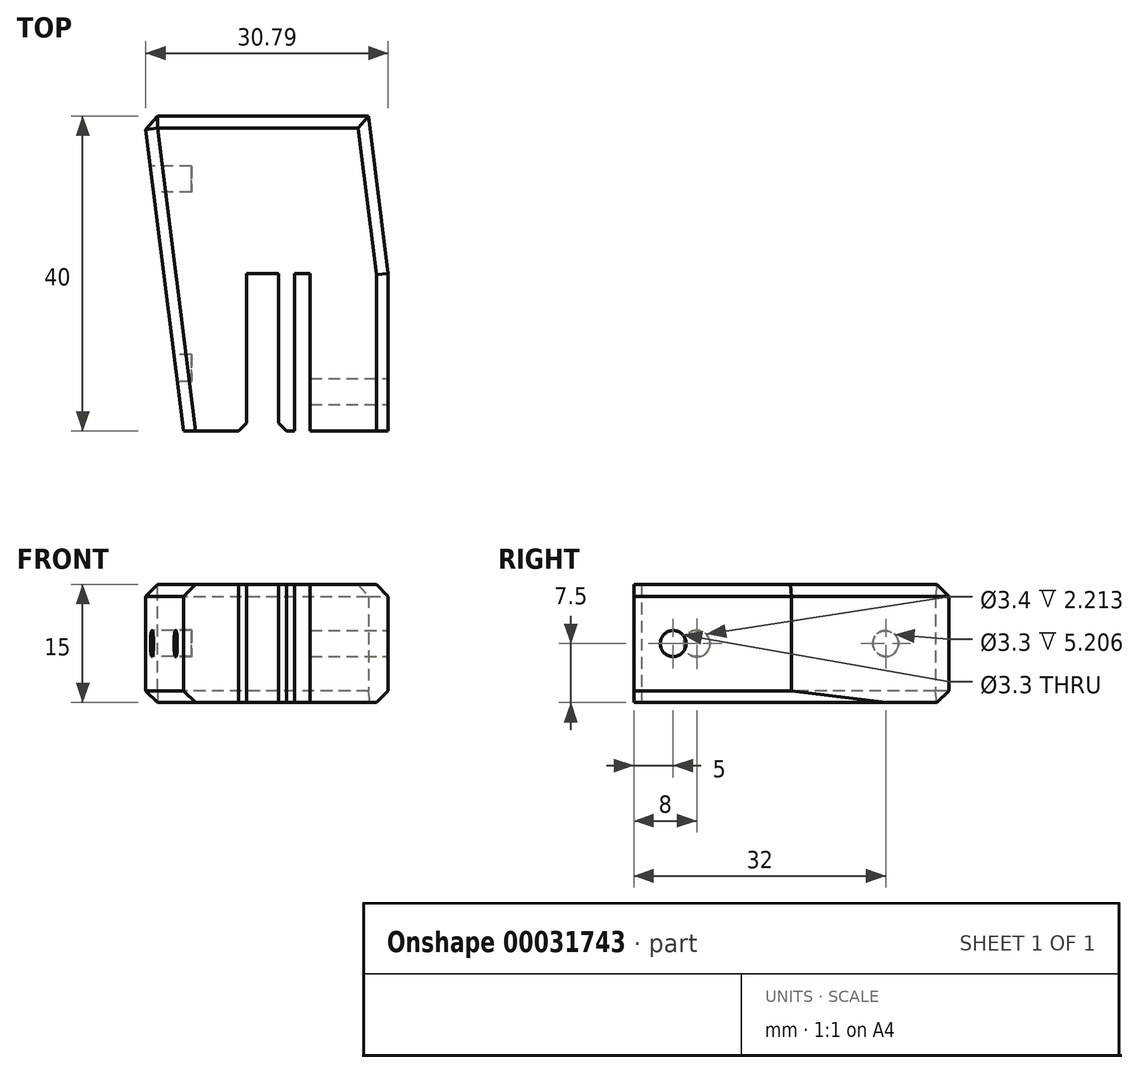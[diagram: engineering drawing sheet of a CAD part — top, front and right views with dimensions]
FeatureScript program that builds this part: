
annotation { "Feature Type Name" : "Feature", "Feature Type Description" : "" }
export const myFeature = defineFeature(function(context is Context, id is Id, definition is map)
    precondition{}
    {
        {
            var Q0;
            Q0=qCreatedBy(makeId("Top.planeOp"),FACE);
            var sketch = newSketch(context, id + "F0", { "sketchPlane" : qUnion([Q0])});
            skLineSegment(sketch, "E0", {"start": v(3, 40) * mm, "end": v(34, 40) * mm});
            skLineSegment(sketch, "E1", {"start": v(34, 40) * mm, "end": v(34, 0) * mm});
            skLineSegment(sketch, "E2", {"start": v(34, 0) * mm, "end": v(24.1, 0) * mm});
            skLineSegment(sketch, "E3", {"start": v(24.1, 0) * mm, "end": v(24.1, 20) * mm});
            skLineSegment(sketch, "E4", {"start": v(24.1, 20) * mm, "end": v(22.1, 20) * mm});
            skLineSegment(sketch, "E5", {"start": v(22.1, 20) * mm, "end": v(22.1, 0) * mm});
            skLineSegment(sketch, "E6", {"start": v(22.1, 0) * mm, "end": v(20.1, 0) * mm});
            skLineSegment(sketch, "E7", {"start": v(20.1, 0) * mm, "end": v(20.1, 20) * mm});
            skLineSegment(sketch, "E8", {"start": v(20.1, 20) * mm, "end": v(16, 20) * mm});
            skLineSegment(sketch, "E9", {"start": v(16, 20) * mm, "end": v(16, 0) * mm});
            skLineSegment(sketch, "E10", {"start": v(16, 0) * mm, "end": v(8, 0) * mm});
            skLineSegment(sketch, "E11", {"start": v(8, 0) * mm, "end": v(3, 40) * mm});
            skPoint(sketch, "E12.orphan", {"position": v(0, 0) * mm});
            skSolve(sketch);
        }
        {
            var Q0;
            Q0 = qSketchRegion(id + "F0", true);
            extrude(context, id + "F1", {"entities" : qUnion([Q0]), "depth" : 15 * mm});
        }
        {
            var Q0;
            Q0=qCreatedBy(makeId("Right.planeOp"),FACE);
            var sketch = newSketch(context, id + "F2", { "sketchPlane" : qUnion([Q0])});
            skCircle(sketch, "E13", {"center": v(32, 7.5) * mm, "radius": 1.65 * mm});
            skCircle(sketch, "E14", {"center": v(8, 7.5) * mm, "radius": 1.7 * mm});
            skSolve(sketch);
        }
        {
            var Q0;
            Q0=makeQuery(id+"F2.imprint","IMPRINT",FACE,{"disambiguationData":[TD([[makeQuery(id+"F2.imprint","IMPRINT",EDGE,{"derivedFrom":sQuery(id+"F2.wireOp",EDGE,"E13")}),1.0]])]});
            var Q1;
            Q1=makeQuery(id+"F2.imprint","IMPRINT",FACE,{"disambiguationData":[TD([[makeQuery(id+"F2.imprint","IMPRINT",EDGE,{"derivedFrom":sQuery(id+"F2.wireOp",EDGE,"E14")}),1.0]])]});
            extrude(context, id + "F3", {"entities" : qUnion([Q0, Q1]), "operationType" : NewBodyOperationType.REMOVE, "depth" : 9 * mm});
        }
        {
            var Q0;
            Q0=makeQuery(id+"F1.opExtrude","CAP_FACE",FACE,{"disambiguationData":[OSD([sQuery(id+"F0.wireOp",EDGE,"E0"),sQuery(id+"F0.wireOp",EDGE,"E1"),sQuery(id+"F0.wireOp",EDGE,"E2"),sQuery(id+"F0.wireOp",EDGE,"E3"),sQuery(id+"F0.wireOp",EDGE,"E4"),sQuery(id+"F0.wireOp",EDGE,"E5"),sQuery(id+"F0.wireOp",EDGE,"E6"),sQuery(id+"F0.wireOp",EDGE,"E7"),sQuery(id+"F0.wireOp",EDGE,"E8"),sQuery(id+"F0.wireOp",EDGE,"E9"),sQuery(id+"F0.wireOp",EDGE,"E10"),sQuery(id+"F0.wireOp",EDGE,"E11")])],"isStart":true});
            var sketch = newSketch(context, id + "F4", { "sketchPlane" : qUnion([Q0])});
            skLineSegment(sketch, "E15", {"start": v(31.5, -40) * mm, "end": v(34, -20) * mm});
            skLineSegment(sketch, "E16", {"start": v(34, -20) * mm, "end": v(34, -40) * mm});
            skLineSegment(sketch, "E17", {"start": v(34, -40) * mm, "end": v(31.5, -40) * mm});
            skSolve(sketch);
        }
        {
            var Q0;
            Q0=makeQuery(id+"F4.imprint","IMPRINT",FACE,{"disambiguationData":[TD([[makeQuery(id+"F4.imprint","IMPRINT",EDGE,{"derivedFrom":sQuery(id+"F4.wireOp",EDGE,"E15")}),-1.0]])]});
            extrude(context, id + "F5", {"entities" : qUnion([Q0]), "operationType" : NewBodyOperationType.REMOVE, "oppositeDirection" : true, "depth" : 25 * mm});
        }
        {
            var Q0;
            Q0=makeQuery(id+"F1.opExtrude","SWEPT_FACE",FACE,{"disambiguationData":[OSD([sQuery(id+"F0.wireOp",EDGE,"E1")])]});
            var sketch = newSketch(context, id + "F6", { "sketchPlane" : qUnion([Q0])});
            skCircle(sketch, "E18", {"center": v(5, 7.5) * mm, "radius": 1.65 * mm});
            skSolve(sketch);
        }
        {
            var Q0;
            Q0=makeQuery(id+"F6.imprint","IMPRINT",FACE,{"disambiguationData":[TD([[makeQuery(id+"F6.imprint","IMPRINT",EDGE,{"derivedFrom":sQuery(id+"F6.wireOp",EDGE,"E18")}),1.0]])]});
            extrude(context, id + "F7", {"entities" : qUnion([Q0]), "operationType" : NewBodyOperationType.REMOVE, "endBound" : BoundingType.UP_TO_NEXT, "oppositeDirection" : true, "depth" : 25 * mm});
        }
        {
            var Q0;
            Q0=makeQuery(id+"F1.opExtrude","CAP_EDGE",EDGE,{"disambiguationData":[OSD([sQuery(id+"F0.wireOp",EDGE,"E0")])],"isStart":false});
            var Q1;
            Q1=makeQuery(id+"F1.opExtrude","CAP_EDGE",EDGE,{"disambiguationData":[OSD([sQuery(id+"F0.wireOp",EDGE,"E0")])],"isStart":true});
            var Q2;
            Q2=makeQuery(id+"F1.opExtrude","CAP_EDGE",EDGE,{"disambiguationData":[OSD([sQuery(id+"F0.wireOp",EDGE,"E11")])],"isStart":true});
            var Q3;
            Q3=makeQuery(id+"F1.opExtrude","CAP_EDGE",EDGE,{"disambiguationData":[OSD([sQuery(id+"F0.wireOp",EDGE,"E11")])],"isStart":false});
            var Q4;
            Q4=makeQuery(id+"F1.opExtrude","SWEPT_EDGE",EDGE,{"disambiguationData":[OSD([sQuery(id+"F0.wireOp",EDGE,"E0"),sQuery(id+"F0.wireOp",EDGE,"E11")])]});
            var Q5;
            Q5=makeQuery(id+"F5.boolean.opBoolean","COPY",EDGE,{"derivedFrom":makeQuery(id+"F5.opExtrude","CAP_EDGE",EDGE,{"disambiguationData":[OSD([sQuery(id+"F4.wireOp",EDGE,"E15")])],"isStart":true})});
            var Q6;
            Q6=makeQuery(id+"F1.opExtrude","CAP_EDGE",EDGE,{"disambiguationData":[OSD([sQuery(id+"F0.wireOp",EDGE,"E1")])],"isStart":true});
            var Q7;
            Q7=makeQuery(id+"F1.opExtrude","CAP_EDGE",EDGE,{"disambiguationData":[OSD([sQuery(id+"F0.wireOp",EDGE,"E1")])],"isStart":false});
            var Q8;
            Q8=makeQuery(id+"F5.boolean.opBoolean","INTERSECT",EDGE,{"derivedFrom":[makeQuery(id+"F1.opExtrude","CAP_FACE",FACE,{"disambiguationData":[OSD([sQuery(id+"F0.wireOp",EDGE,"E0"),sQuery(id+"F0.wireOp",EDGE,"E1"),sQuery(id+"F0.wireOp",EDGE,"E2"),sQuery(id+"F0.wireOp",EDGE,"E3"),sQuery(id+"F0.wireOp",EDGE,"E4"),sQuery(id+"F0.wireOp",EDGE,"E5"),sQuery(id+"F0.wireOp",EDGE,"E6"),sQuery(id+"F0.wireOp",EDGE,"E7"),sQuery(id+"F0.wireOp",EDGE,"E8"),sQuery(id+"F0.wireOp",EDGE,"E9"),sQuery(id+"F0.wireOp",EDGE,"E10"),sQuery(id+"F0.wireOp",EDGE,"E11")])],"isStart":false}),makeQuery(id+"F5.opExtrude","SWEPT_FACE",FACE,{"disambiguationData":[OSD([sQuery(id+"F4.wireOp",EDGE,"E15")])]})]});
            var Q9;
            Q9=makeQuery(id+"F5.boolean.opBoolean","COPY",EDGE,{"derivedFrom":makeQuery(id+"F5.opExtrude","SWEPT_EDGE",EDGE,{"disambiguationData":[OSD([sQuery(id+"F0.wireOp",EDGE,"E0"),sQuery(id+"F4.wireOp",EDGE,"E15"),sQuery(id+"F4.wireOp",EDGE,"E17")])]})});
            chamfer(context, id + "F8", {"entities" : qUnion([Q0, Q1, Q2, Q3, Q4, Q5, Q6, Q7, Q8, Q9]), "width" : 1.5 * mm, "tangentPropagation" : true});
        }
        {
            var Q0;
            Q0=makeQuery(id+"F1.opExtrude","SWEPT_EDGE",EDGE,{"disambiguationData":[OSD([sQuery(id+"F0.wireOp",EDGE,"E6"),sQuery(id+"F0.wireOp",EDGE,"E7")])]});
            var Q1;
            Q1=makeQuery(id+"F1.opExtrude","SWEPT_EDGE",EDGE,{"disambiguationData":[OSD([sQuery(id+"F0.wireOp",EDGE,"E9"),sQuery(id+"F0.wireOp",EDGE,"E10")])]});
            chamfer(context, id + "F9", {"entities" : qUnion([Q0, Q1]), "width" : 1 * mm, "tangentPropagation" : true});
        }
    });
